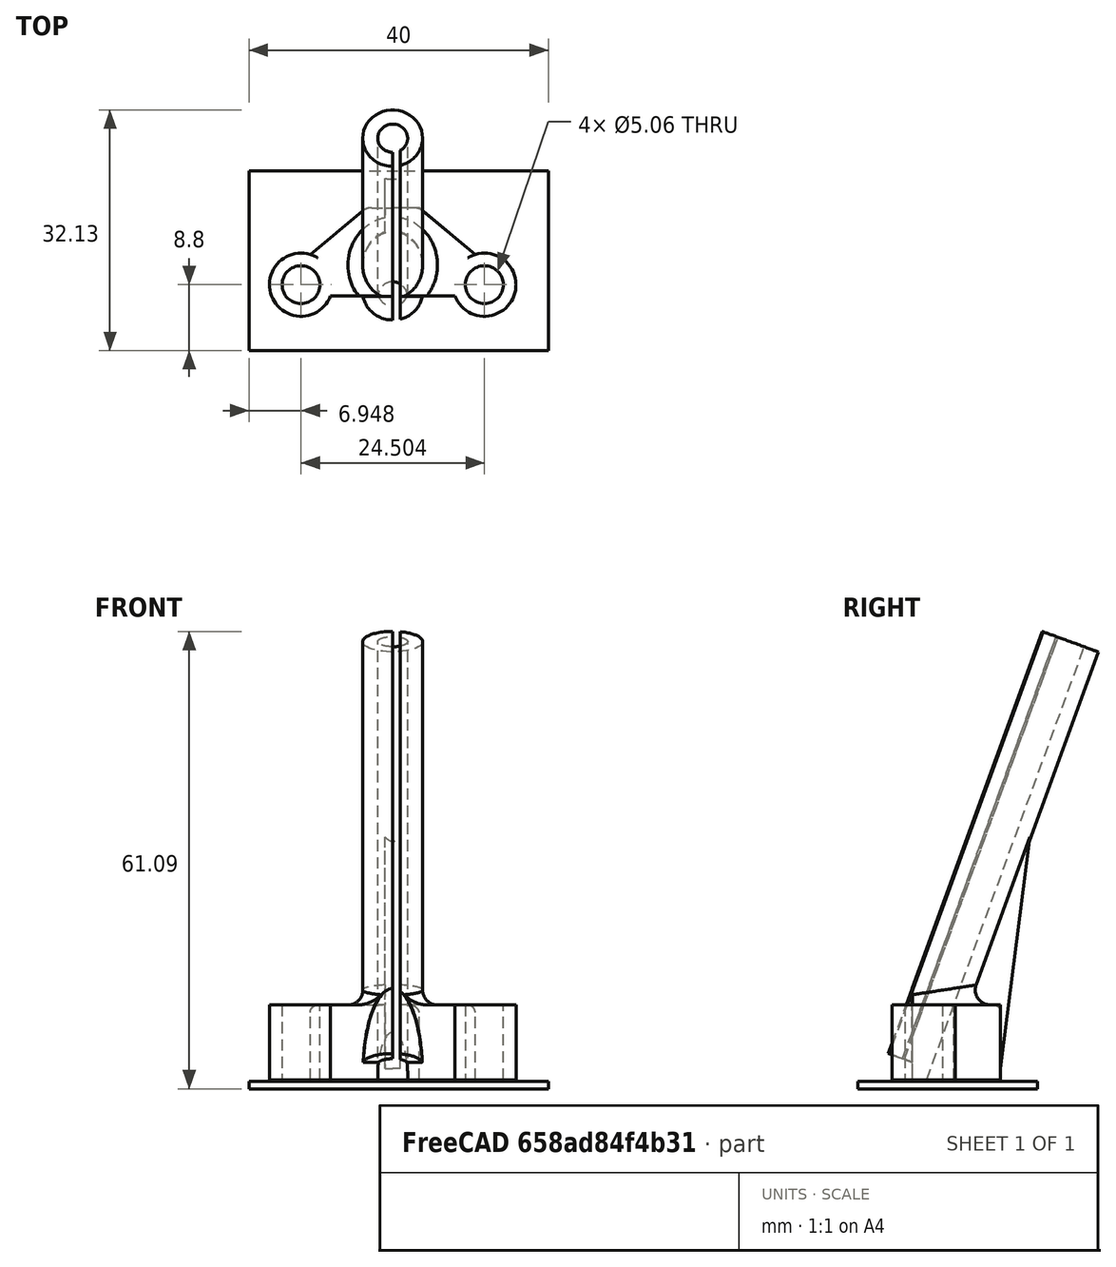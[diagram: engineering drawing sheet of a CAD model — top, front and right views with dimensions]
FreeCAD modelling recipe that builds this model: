
FCSTD DOCUMENT  (FreeCAD 0.19R24267 +99 (Git))
Label: O3天线
License: All rights reserved
LicenseURL: http://en.wikipedia.org/wiki/All_rights_reserved
objects: Part::Fillet×5, Part::Cut×3, Part::Box×3, Mesh::Feature×2, Sketcher::SketchObject×2, PartDesign::Pad×2, PartDesign::Body×2, Part::Cylinder×2, Part::Fuse×2, App::MeasureDistance×1
note: 23 computed .brp shape members not serialized (recipe doc carries the construction recipe); baked Part::Feature solids carry a one-line shape summary decoded from their .brp

FEATURE [Mesh::Feature] FPVCycle_Glide_DJI_O3_Ait_Unit_Antenna_Mount
  Placement = pos=(-18,-3,0) rot=(0,0,1;0rad)
FEATURE [Mesh::Feature] GEPRC_MK5_BODYBN220_SMA_T  label="GEPRC-MK5-BODYBN220+SMA+T"
FEATURE [Sketcher::SketchObject] Sketch
  FullyConstrained = false
  MapMode = 5
  Support = -> [XY_Plane]
  sketch-geometry (10):
    g0: Circle CenterX=-12.2518 CenterY=0 CenterZ=0 NormalX=0 NormalY=0 NormalZ=1 AngleXU=0 Radius=2.5279
    g1: ArcOfCircle CenterX=-12.2518 CenterY=0 CenterZ=0 NormalX=0 NormalY=0 NormalZ=1 AngleXU=0 Radius=4.21759 StartAngle=1.27545 EndAngle=5.91917
    g2: LineSegment StartX=-11.0241 StartY=4.03498 StartZ=0 EndX=-3.53405 EndY=10.2761 EndZ=0
    g3: LineSegment StartX=-3.53405 StartY=10.2761 StartZ=0 EndX=0 EndY=10.2761 EndZ=0
    g4: LineSegment StartX=-8.31052 StartY=-1.50159 StartZ=0 EndX=0 EndY=-1.50159 EndZ=0
    g5: Circle CenterX=12.2518 CenterY=0 CenterZ=0 NormalX=0 NormalY=0 NormalZ=1 AngleXU=0 Radius=2.5279
    g6: ArcOfCircle CenterX=12.2518 CenterY=0 CenterZ=0 NormalX=0 NormalY=0 NormalZ=1 AngleXU=0 Radius=4.21759 StartAngle=3.50561 EndAngle=8.14932
    g7: LineSegment StartX=11.0241 StartY=4.03498 StartZ=0 EndX=3.53405 EndY=10.2761 EndZ=0
    g8: LineSegment StartX=3.53405 StartY=10.2761 StartZ=0 EndX=0 EndY=10.2761 EndZ=0
    g9: LineSegment StartX=8.31052 StartY=-1.50159 StartZ=0 EndX=0 EndY=-1.50159 EndZ=0
  constraints (15):
    c: PointOnObject(g0,g-1)
    c: Coincident(g1,g0)
    c: Coincident(g2,g3)
    c: PointOnObject(g3,g-2)
    c: Horizontal(g3)
    c: Coincident(g1,g2)
    c: Coincident(g4,g1)
    c: PointOnObject(g4,g-2)
    c: Horizontal(g4)
    c: Coincident(g6,g5)
    c: Coincident(g7,g8)
    c: Horizontal(g8)
    c: Coincident(g6,g7)
    c: Coincident(g9,g6)
    c: Horizontal(g9)
FEATURE [PartDesign::Pad] Pad
  Direction = (1,1,1)
  Length = 10
  Length2 = 100
  Profile = -> Sketch
  Type = 0
FEATURE [PartDesign::Body] Body
  Group = -> [Sketch,Pad]
  Origin = -> Origin
  Tip = -> Pad
FEATURE [Part::Cylinder] Cylinder  label="圆柱体"
  Angle = 360
  AttacherType = Attacher::AttachEngine3D
  Height = 67
  Placement = pos=(0,-2.31808,-1.61877) rot=(1,0,0;5.93412rad)
  Radius = 2
FEATURE [Part::Cylinder] Cylinder001  label="圆柱体001"
  Angle = 360
  AttacherType = Attacher::AttachEngine3D
  Height = 60
  Placement = pos=(0,-0.95,2.14) rot=(-1,0,0;0.349066rad)
  Radius = 4
FEATURE [Part::Fuse] Fusion
  Base = -> Body
  Tool = -> Cylinder001
FEATURE [Part::Cut] Cut
  Base = -> Fusion
  Tool = -> Cylinder
FEATURE [Part::Box] Box  label="立方体"
  AttacherType = Attacher::AttachEngine3D
  Height = 62
  Length = 1
  Placement = pos=(0,-5.29614,2.99181) rot=(1,0,0;5.93412rad)
  Width = 4
FEATURE [Part::Cut] Cut001
  Base = -> Cut
  Tool = -> Box
FEATURE [Part::Fillet] Fillet
  Base = -> Cut001
  Edges = 1 edges r=2: [Edge23]
FEATURE [Sketcher::SketchObject] Sketch001
  FullyConstrained = false
  MapMode = 5
  Placement = pos=(0,0,0) rot=(0.57735,0.57735,0.57735;2.0944rad)
  Support = -> [YZ_Plane001]
  sketch-geometry (4):
    g0: LineSegment StartX=11.126 StartY=25.1273 StartZ=0 EndX=5.15667 EndY=9.78067 EndZ=0
    g1: LineSegment StartX=5.15667 StartY=9.78067 StartZ=0 EndX=10.0866 EndY=0 EndZ=0
    g2: LineSegment StartX=10.0866 StartY=0 StartZ=0 EndX=14.2147 EndY=32.6165 EndZ=0
    g3: LineSegment StartX=14.2147 StartY=32.6165 StartZ=0 EndX=11.126 EndY=25.1273 EndZ=0
  constraints (5):
    c: Coincident(g0,g1)
    c: PointOnObject(g1,g-1)
    c: Coincident(g1,g2)
    c: Coincident(g2,g3)
    c: Coincident(g3,g0)
FEATURE [PartDesign::Pad] Pad001
  Direction = (1,1,1)
  Length = 2
  Length2 = 100
  Midplane = true
  Placement = pos=(0,0,0) rot=(0.57735,0.57735,0.57735;2.0944rad)
  Profile = -> Sketch001
  Type = 0
FEATURE [PartDesign::Body] Body001
  Group = -> [Sketch001,Pad001]
  Origin = -> Origin001
  Tip = -> Pad001
FEATURE [Part::Fuse] Fusion001
  Base = -> Fillet
  Tool = -> Body001
FEATURE [Part::Fillet] Fillet001
  Base = -> Fusion001
  Edges = 1 edges r=2: [Edge13]
FEATURE [Part::Fillet] Fillet002
  Base = -> Fillet001
  Edges = 1 edges r=2: [Edge24]
FEATURE [Part::Fillet] Fillet003
  Base = -> Fillet001
  Edges = 2 edges r=1: [Edge25,Edge38]
FEATURE [Part::Fillet] Fillet004
  Base = -> Fillet002
  Edges = 2 edges r=1: [Edge22,Edge34]
FEATURE [Part::Box] Box001  label="立方体001"
  AttacherType = Attacher::AttachEngine3D
  Height = 18
  Length = 10
  Placement = pos=(-4.48,-1.55,0) rot=(0,0,-1;1.5708rad)
  Width = 10
FEATURE [Part::Cut] Cut002
  Base = -> Fillet004
  Tool = -> Box001
FEATURE [App::MeasureDistance] Distance  label="Distance: 51.15 mm"
  Distance = 51.149
  P1 = (1.03973,15.9413,59.8284)
  P2 = (1.09515,-1.5387,11.759)
FEATURE [Part::Box] Box002  label="立方体002"
  AttacherType = Attacher::AttachEngine3D
  Height = 1
  Length = 40
  Placement = pos=(-19.2,-8.8,-1.2) rot=(0,0,1;0rad)
  Width = 24
